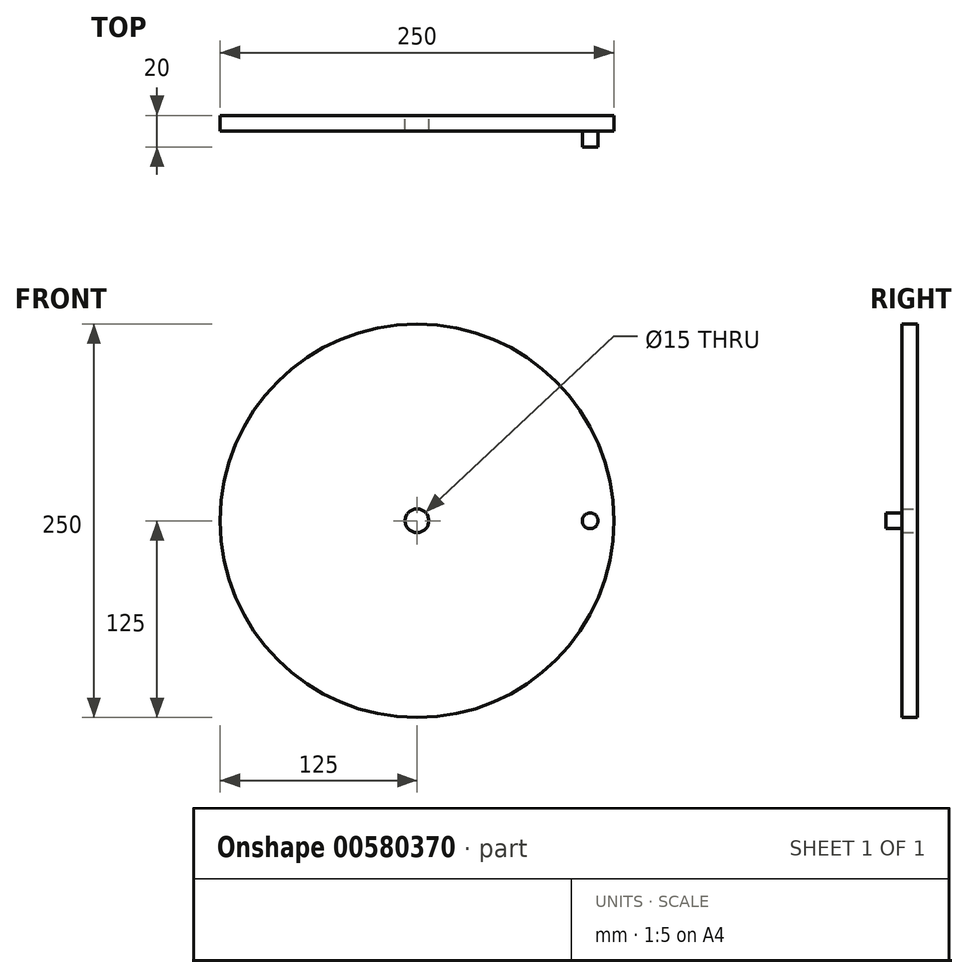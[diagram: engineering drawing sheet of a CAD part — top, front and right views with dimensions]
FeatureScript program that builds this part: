
annotation { "Feature Type Name" : "Feature", "Feature Type Description" : "" }
export const myFeature = defineFeature(function(context is Context, id is Id, definition is map)
    precondition{}
    {
        {
            var Q0;
            Q0=qCreatedBy(makeId("Front.planeOp"),FACE);
            var sketch = newSketch(context, id + "F0", { "sketchPlane" : qUnion([Q0])});
            skCircle(sketch, "E0", {"center": v(0, 0) * mm, "radius": 125 * mm});
            skCircle(sketch, "E1", {"center": v(0, 0) * mm, "radius": 7.5 * mm});
            skSolve(sketch);
        }
        {
            var Q0;
            Q0=makeQuery(id+"F0.imprint","IMPRINT",FACE,{"disambiguationData":[TD([[makeQuery(id+"F0.imprint","IMPRINT",EDGE,{"derivedFrom":sQuery(id+"F0.wireOp",EDGE,"E0")}),1.0]])]});
            extrude(context, id + "F1", {"entities" : qUnion([Q0]), "depth" : 10 * mm, "offsetDistance" : 25 * mm});
        }
        {
            var Q0;
            Q0=makeQuery(id+"F1.opExtrude","CAP_FACE",FACE,{"disambiguationData":[OSD([sQuery(id+"F0.wireOp",EDGE,"E0"),sQuery(id+"F0.wireOp",EDGE,"E1")])],"isStart":false});
            var sketch = newSketch(context, id + "F2", { "sketchPlane" : qUnion([Q0])});
            skCircle(sketch, "E2", {"center": v(110, 0) * mm, "radius": 5 * mm});
            skSolve(sketch);
        }
        {
            var Q0;
            Q0 = qSketchRegion(id + "F2", true);
            extrude(context, id + "F3", {"entities" : qUnion([Q0]), "operationType" : NewBodyOperationType.ADD, "depth" : 10 * mm, "offsetDistance" : 25 * mm});
        }
    });
